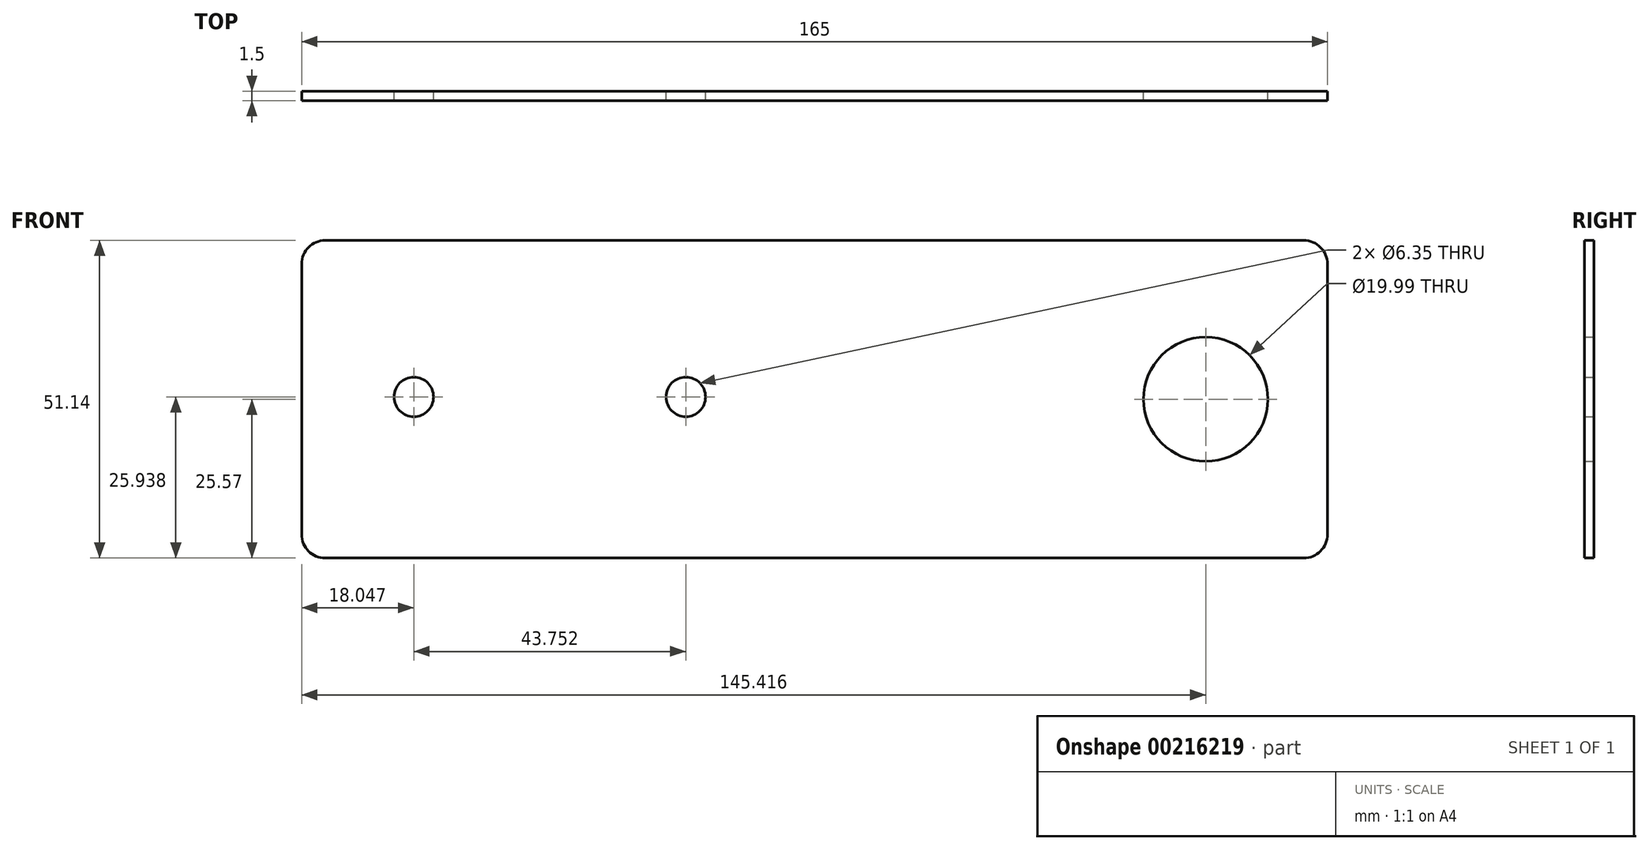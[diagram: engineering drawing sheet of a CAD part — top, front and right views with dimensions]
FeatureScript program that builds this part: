
annotation { "Feature Type Name" : "Feature", "Feature Type Description" : "" }
export const myFeature = defineFeature(function(context is Context, id is Id, definition is map)
    precondition{}
    {
        {
            var Q0;
            Q0=qCreatedBy(makeId("Front.planeOp"),FACE);
            var sketch = newSketch(context, id + "F0", { "sketchPlane" : qUnion([Q0])});
            skLineSegment(sketch, "E0.bottom", {"start": v(78.69, 25.57) * mm, "end": v(-78.69, 25.57) * mm});
            skLineSegment(sketch, "E0.top", {"start": v(78.69, -25.57) * mm, "end": v(-78.69, -25.57) * mm});
            skLineSegment(sketch, "E0.left", {"start": v(82.5, 21.76) * mm, "end": v(82.5, -21.76) * mm});
            skLineSegment(sketch, "E0.right", {"start": v(-82.5, 21.76) * mm, "end": v(-82.5, -21.76) * mm});
            skPoint(sketch, "E0.middle", {"position": v(0, 0) * mm});
            skPoint(sketch, "E1.visualSharp", {"position": v(82.5, 25.57) * mm});
            skArc(sketch, "E1.filletArc", {"start": v(82.5, 21.76) * mm, "mid": v(81.38, 24.45) * mm, "end": v(78.69, 25.57) * mm});
            skPoint(sketch, "E2.visualSharp", {"position": v(82.5, -25.57) * mm});
            skArc(sketch, "E2.filletArc", {"start": v(78.69, -25.57) * mm, "mid": v(81.38, -24.45) * mm, "end": v(82.5, -21.76) * mm});
            skPoint(sketch, "E3.visualSharp", {"position": v(-82.5, -25.57) * mm});
            skArc(sketch, "E3.filletArc", {"start": v(-82.5, -21.76) * mm, "mid": v(-81.38, -24.45) * mm, "end": v(-78.69, -25.57) * mm});
            skPoint(sketch, "E4.visualSharp", {"position": v(-82.5, 25.57) * mm});
            skArc(sketch, "E4.filletArc", {"start": v(-78.69, 25.57) * mm, "mid": v(-81.38, 24.45) * mm, "end": v(-82.5, 21.76) * mm});
            skPoint(sketch, "E5.centerSnap0", {"position": v(82.5, 0) * mm});
            skLineSegment(sketch, "E6", {"start": v(-82.5, 0) * mm, "end": v(-82.5, 0.37) * mm, "construction": true});
            skLineSegment(sketch, "E7", {"start": v(-82.5, 0.37) * mm, "end": v(-64.45, 0.37) * mm, "construction": true});
            skCircle(sketch, "E8", {"center": v(-64.45, 0.37) * mm, "radius": 3.18 * mm});
            skLineSegment(sketch, "E9", {"start": v(-82.5, 0.37) * mm, "end": v(-20.7, 0.37) * mm, "construction": true});
            skCircle(sketch, "E10", {"center": v(-20.7, 0.37) * mm, "radius": 3.18 * mm});
            skLineSegment(sketch, "E11", {"start": v(82.5, 0) * mm, "end": v(62.92, 0) * mm, "construction": true});
            skCircle(sketch, "E12", {"center": v(62.92, 0) * mm, "radius": 10 * mm});
            skSolve(sketch);
        }
        {
            var Q0;
            Q0=makeQuery(id+"F0.imprint","IMPRINT",FACE,{"disambiguationData":[TD([[makeQuery(id+"F0.imprint","IMPRINT",EDGE,{"derivedFrom":sQuery(id+"F0.wireOp",EDGE,"E0.bottom")}),1.0]])]});
            extrude(context, id + "F1", {"entities" : qUnion([Q0]), "endBound" : BoundingType.SYMMETRIC, "depth" : 1.5 * mm});
        }
    });
